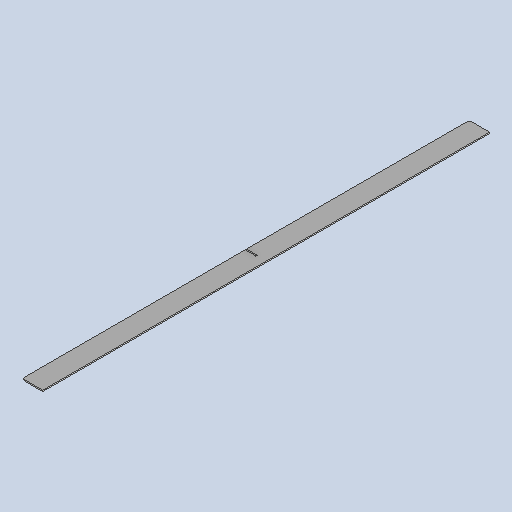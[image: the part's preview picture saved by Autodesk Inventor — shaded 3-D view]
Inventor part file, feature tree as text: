
AUTODESK INVENTOR PART (.ipt)
format: ipt  version: 2025 (Build 290162010, 162A)  size: 295,424 bytes
history: native  units: mm
features: other x3, sheet_metal_op x1, chamfer x1, sketch x1
ambient origin geometry x8: Origin, YZ Plane, XZ Plane, XY Plane, X Axis, Y Axis, Z Axis, Center Point
bodies: Body1 (feature_tree)
feature tree (6):
  other  "BSH 505 amplifier"
  sheet_metal_op  "Face2"
  chamfer  "Corner Round1"
  sketch  "Sketch1"  dims[d15=3.0mm d17=1098.0mm d18=50.0mm d19=3.0mm d20=26.0mm d21=6.0mm]
  other  "Plate2"
  other  "Definition1"
